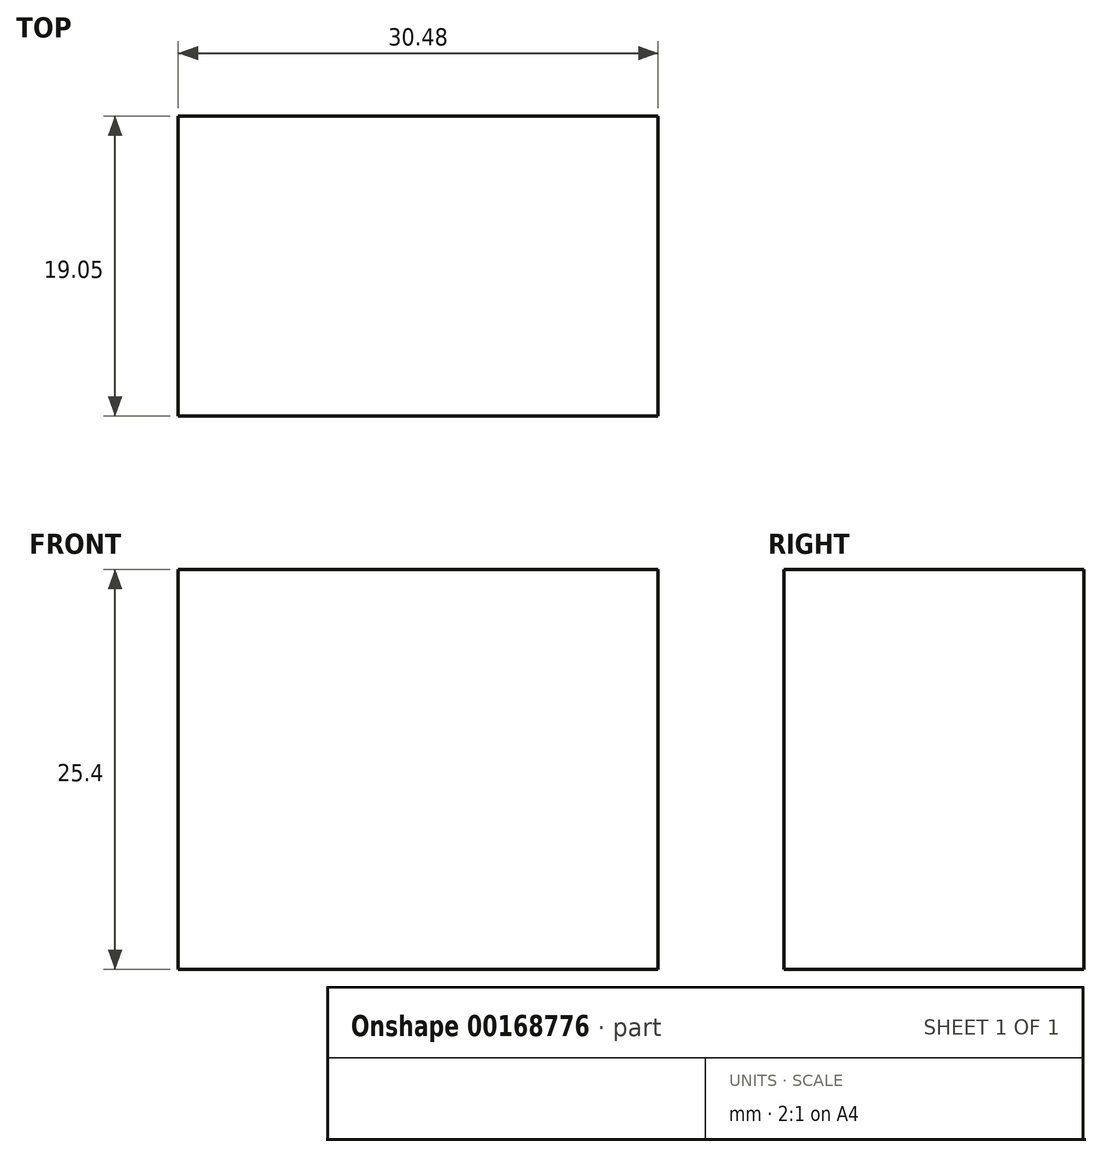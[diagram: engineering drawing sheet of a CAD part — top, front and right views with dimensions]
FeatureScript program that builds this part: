
annotation { "Feature Type Name" : "Feature", "Feature Type Description" : "" }
export const myFeature = defineFeature(function(context is Context, id is Id, definition is map)
    precondition{}
    {
        {
            var Q0;
            Q0=qCreatedBy(makeId("Front.planeOp"),FACE);
            var sketch = newSketch(context, id + "F0", { "sketchPlane" : qUnion([Q0])});
            skLineSegment(sketch, "E0.bottom", {"start": v(9.52, -12.7) * mm, "end": v(-9.53, -12.7) * mm});
            skLineSegment(sketch, "E0.top", {"start": v(9.52, 12.7) * mm, "end": v(-9.53, 12.7) * mm});
            skLineSegment(sketch, "E0.left", {"start": v(9.52, -12.7) * mm, "end": v(9.52, 12.7) * mm});
            skLineSegment(sketch, "E0.right", {"start": v(-9.53, -12.7) * mm, "end": v(-9.53, 12.7) * mm});
            skPoint(sketch, "E0.middle", {"position": v(0, 0) * mm});
            skLineSegment(sketch, "E1", {"start": v(-9.53, 11.43) * mm, "end": v(9.52, 11.43) * mm});
            skLineSegment(sketch, "E2", {"start": v(-9.53, 10.16) * mm, "end": v(9.52, 10.16) * mm});
            skLineSegment(sketch, "E3", {"start": v(-9.53, 8.89) * mm, "end": v(9.52, 8.89) * mm});
            skLineSegment(sketch, "E4", {"start": v(-9.53, 7.62) * mm, "end": v(9.52, 7.62) * mm});
            skLineSegment(sketch, "E5", {"start": v(-9.53, 6.35) * mm, "end": v(9.52, 6.35) * mm});
            skLineSegment(sketch, "E6", {"start": v(-9.53, 5.08) * mm, "end": v(9.52, 5.08) * mm});
            skLineSegment(sketch, "E7", {"start": v(-9.53, 3.8) * mm, "end": v(9.53, 3.8) * mm});
            skLineSegment(sketch, "E8", {"start": v(-9.53, 2.54) * mm, "end": v(9.53, 2.54) * mm});
            skLineSegment(sketch, "E9", {"start": v(-9.53, 1.27) * mm, "end": v(9.53, 1.27) * mm});
            skLineSegment(sketch, "E10", {"start": v(-9.53, 0) * mm, "end": v(9.52, 0) * mm});
            skLineSegment(sketch, "E11", {"start": v(-9.53, -1.27) * mm, "end": v(9.53, -1.27) * mm});
            skLineSegment(sketch, "E12", {"start": v(-9.53, -2.54) * mm, "end": v(9.53, -2.54) * mm});
            skLineSegment(sketch, "E13", {"start": v(-9.53, -3.81) * mm, "end": v(9.53, -3.81) * mm});
            skLineSegment(sketch, "E14", {"start": v(-9.53, -5.08) * mm, "end": v(9.53, -5.08) * mm});
            skLineSegment(sketch, "E15", {"start": v(-9.52, -6.35) * mm, "end": v(9.53, -6.35) * mm});
            skLineSegment(sketch, "E16", {"start": v(-9.53, -7.62) * mm, "end": v(9.53, -7.62) * mm});
            skLineSegment(sketch, "E17", {"start": v(-9.52, -8.9) * mm, "end": v(9.53, -8.9) * mm});
            skLineSegment(sketch, "E18", {"start": v(-9.53, -10.16) * mm, "end": v(9.53, -10.16) * mm});
            skLineSegment(sketch, "E19", {"start": v(-9.52, -11.43) * mm, "end": v(9.53, -11.43) * mm});
            skLineSegment(sketch, "E20", {"start": v(-9.52, -10.16) * mm, "end": v(9.53, -10.16) * mm});
            skSolve(sketch);
        }
        {
            var Q0;
            Q0=sQuery(id+"F0.wireOp",EDGE,"E0.left");
            var Q1;
            Q1=sQuery(id+"F0.wireOp",EDGE,"E0.top");
            var Q2;
            Q2=sQuery(id+"F0.wireOp",EDGE,"E0.right");
            var Q3;
            Q3=sQuery(id+"F0.wireOp",EDGE,"E0.bottom");
            extrude(context, id + "F1", {"bodyType" : ToolBodyType.SURFACE, "surfaceEntities" : qUnion([Q0, Q1, Q2, Q3]), "endBound" : BoundingType.SYMMETRIC, "depth" : 25.4 * mm});
        }
        {
            var Q0;
            Q0=sQuery(id+"F0.wireOp",EDGE,"E1");
            var Q1;
            Q1=sQuery(id+"F0.wireOp",EDGE,"E2");
            var Q2;
            Q2=sQuery(id+"F0.wireOp",EDGE,"E3");
            var Q3;
            Q3=sQuery(id+"F0.wireOp",EDGE,"E4");
            var Q4;
            Q4=sQuery(id+"F0.wireOp",EDGE,"E5");
            var Q5;
            Q5=sQuery(id+"F0.wireOp",EDGE,"E6");
            var Q6;
            Q6=sQuery(id+"F0.wireOp",EDGE,"E7");
            var Q7;
            Q7=sQuery(id+"F0.wireOp",EDGE,"E8");
            var Q8;
            Q8=sQuery(id+"F0.wireOp",EDGE,"E9");
            var Q9;
            Q9=sQuery(id+"F0.wireOp",EDGE,"E10");
            var Q10;
            Q10=sQuery(id+"F0.wireOp",EDGE,"E11");
            var Q11;
            Q11=sQuery(id+"F0.wireOp",EDGE,"E12");
            var Q12;
            Q12=sQuery(id+"F0.wireOp",EDGE,"E13");
            var Q13;
            Q13=sQuery(id+"F0.wireOp",EDGE,"E14");
            var Q14;
            Q14=sQuery(id+"F0.wireOp",EDGE,"E15");
            var Q15;
            Q15=sQuery(id+"F0.wireOp",EDGE,"E16");
            var Q16;
            Q16=sQuery(id+"F0.wireOp",EDGE,"E17");
            var Q17;
            Q17=sQuery(id+"F0.wireOp",EDGE,"E18");
            var Q18;
            Q18=sQuery(id+"F0.wireOp",EDGE,"E19");
            extrude(context, id + "F2", {"bodyType" : ToolBodyType.SURFACE, "surfaceEntities" : qUnion([Q0, Q1, Q2, Q3, Q4, Q5, Q6, Q7, Q8, Q9, Q10, Q11, Q12, Q13, Q14, Q15, Q16, Q17, Q18]), "endBound" : BoundingType.SYMMETRIC, "depth" : 20.32 * mm});
        }
        {
            var Q0;
            {var subQ0=sQuery(id+"F0.wireOp",EDGE,"E0.top");Q0=makeQuery(id+"F0.imprint","IMPRINT",FACE,{"disambiguationData":[TD([[makeQuery(id+"F0.imprint","IMPRINT",EDGE,{"derivedFrom":subQ0}),1.0]])]});}
            var Q1;
            {var subQ0=sQuery(id+"F0.wireOp",EDGE,"E1");Q1=makeQuery(id+"F0.imprint","IMPRINT",FACE,{"disambiguationData":[TD([[makeQuery(id+"F0.imprint","IMPRINT",EDGE,{"derivedFrom":subQ0}),-1.0]])]});}
            var Q2;
            {var subQ0=sQuery(id+"F0.wireOp",EDGE,"E2");Q2=makeQuery(id+"F0.imprint","IMPRINT",FACE,{"disambiguationData":[TD([[makeQuery(id+"F0.imprint","IMPRINT",EDGE,{"derivedFrom":subQ0}),-1.0]])]});}
            var Q3;
            {var subQ0=sQuery(id+"F0.wireOp",EDGE,"E3");Q3=makeQuery(id+"F0.imprint","IMPRINT",FACE,{"disambiguationData":[TD([[makeQuery(id+"F0.imprint","IMPRINT",EDGE,{"derivedFrom":subQ0}),-1.0]])]});}
            var Q4;
            {var subQ0=sQuery(id+"F0.wireOp",EDGE,"E4");Q4=makeQuery(id+"F0.imprint","IMPRINT",FACE,{"disambiguationData":[TD([[makeQuery(id+"F0.imprint","IMPRINT",EDGE,{"derivedFrom":subQ0}),-1.0]])]});}
            var Q5;
            {var subQ0=sQuery(id+"F0.wireOp",EDGE,"E5");Q5=makeQuery(id+"F0.imprint","IMPRINT",FACE,{"disambiguationData":[TD([[makeQuery(id+"F0.imprint","IMPRINT",EDGE,{"derivedFrom":subQ0}),-1.0]])]});}
            var Q6;
            {var subQ0=sQuery(id+"F0.wireOp",EDGE,"E6");Q6=makeQuery(id+"F0.imprint","IMPRINT",FACE,{"disambiguationData":[TD([[makeQuery(id+"F0.imprint","IMPRINT",EDGE,{"derivedFrom":subQ0}),-1.0]])]});}
            var Q7;
            {var subQ0=sQuery(id+"F0.wireOp",EDGE,"E7");Q7=makeQuery(id+"F0.imprint","IMPRINT",FACE,{"disambiguationData":[TD([[makeQuery(id+"F0.imprint","IMPRINT",EDGE,{"derivedFrom":subQ0}),-1.0]])]});}
            var Q8;
            {var subQ0=sQuery(id+"F0.wireOp",EDGE,"E8");Q8=makeQuery(id+"F0.imprint","IMPRINT",FACE,{"disambiguationData":[TD([[makeQuery(id+"F0.imprint","IMPRINT",EDGE,{"derivedFrom":subQ0}),-1.0]])]});}
            var Q9;
            {var subQ0=sQuery(id+"F0.wireOp",EDGE,"E9");Q9=makeQuery(id+"F0.imprint","IMPRINT",FACE,{"disambiguationData":[TD([[makeQuery(id+"F0.imprint","IMPRINT",EDGE,{"derivedFrom":subQ0}),-1.0]])]});}
            var Q10;
            {var subQ0=sQuery(id+"F0.wireOp",EDGE,"E10");Q10=makeQuery(id+"F0.imprint","IMPRINT",FACE,{"disambiguationData":[TD([[makeQuery(id+"F0.imprint","IMPRINT",EDGE,{"derivedFrom":subQ0}),-1.0]])]});}
            var Q11;
            {var subQ0=sQuery(id+"F0.wireOp",EDGE,"E11");Q11=makeQuery(id+"F0.imprint","IMPRINT",FACE,{"disambiguationData":[TD([[makeQuery(id+"F0.imprint","IMPRINT",EDGE,{"derivedFrom":subQ0}),-1.0]])]});}
            var Q12;
            {var subQ0=sQuery(id+"F0.wireOp",EDGE,"E12");Q12=makeQuery(id+"F0.imprint","IMPRINT",FACE,{"disambiguationData":[TD([[makeQuery(id+"F0.imprint","IMPRINT",EDGE,{"derivedFrom":subQ0}),-1.0]])]});}
            var Q13;
            {var subQ0=sQuery(id+"F0.wireOp",EDGE,"E13");Q13=makeQuery(id+"F0.imprint","IMPRINT",FACE,{"disambiguationData":[TD([[makeQuery(id+"F0.imprint","IMPRINT",EDGE,{"derivedFrom":subQ0}),-1.0]])]});}
            var Q14;
            {var subQ0=sQuery(id+"F0.wireOp",EDGE,"E14");Q14=makeQuery(id+"F0.imprint","IMPRINT",FACE,{"disambiguationData":[TD([[makeQuery(id+"F0.imprint","IMPRINT",EDGE,{"derivedFrom":subQ0}),-1.0]])]});}
            var Q15;
            {var subQ0=sQuery(id+"F0.wireOp",EDGE,"E15");Q15=makeQuery(id+"F0.imprint","IMPRINT",FACE,{"disambiguationData":[TD([[makeQuery(id+"F0.imprint","IMPRINT",EDGE,{"derivedFrom":subQ0}),-1.0]])]});}
            var Q16;
            {var subQ0=sQuery(id+"F0.wireOp",EDGE,"E16");Q16=makeQuery(id+"F0.imprint","IMPRINT",FACE,{"disambiguationData":[TD([[makeQuery(id+"F0.imprint","IMPRINT",EDGE,{"derivedFrom":subQ0}),-1.0]])]});}
            var Q17;
            {var subQ0=sQuery(id+"F0.wireOp",EDGE,"E17");Q17=makeQuery(id+"F0.imprint","IMPRINT",FACE,{"disambiguationData":[TD([[makeQuery(id+"F0.imprint","IMPRINT",EDGE,{"derivedFrom":subQ0}),-1.0]])]});}
            var Q18;
            {var subQ0=sQuery(id+"F0.wireOp",EDGE,"E19");Q18=makeQuery(id+"F0.imprint","IMPRINT",FACE,{"disambiguationData":[TD([[makeQuery(id+"F0.imprint","IMPRINT",EDGE,{"derivedFrom":subQ0}),1.0]])]});}
            var Q19;
            {var subQ0=sQuery(id+"F0.wireOp",EDGE,"E0.bottom");Q19=makeQuery(id+"F0.imprint","IMPRINT",FACE,{"disambiguationData":[TD([[makeQuery(id+"F0.imprint","IMPRINT",EDGE,{"derivedFrom":subQ0}),-1.0]])]});}
            extrude(context, id + "F3", {"entities" : qUnion([Q0, Q1, Q2, Q3, Q4, Q5, Q6, Q7, Q8, Q9, Q10, Q11, Q12, Q13, Q14, Q15, Q16, Q17, Q18, Q19]), "endBound" : BoundingType.SYMMETRIC, "depth" : 30.48 * mm});
        }
        {
            var Q0;
            Q0=makeQuery(id+"F2.opExtrude","SWEPT_BODY",BODY,{"disambiguationData":[OSD([sQuery(id+"F0.wireOp",EDGE,"E5")])]});
            var Q1;
            Q1=makeQuery(id+"F1.opExtrude","SWEPT_BODY",BODY,{"disambiguationData":[OSD([sQuery(id+"F0.wireOp",EDGE,"E0.bottom")])]});
            var Q2;
            Q2=makeQuery(id+"F2.opExtrude","SWEPT_BODY",BODY,{"disambiguationData":[OSD([sQuery(id+"F0.wireOp",EDGE,"E6")])]});
            var Q3;
            Q3=makeQuery(id+"F2.opExtrude","SWEPT_BODY",BODY,{"disambiguationData":[OSD([sQuery(id+"F0.wireOp",EDGE,"E7")])]});
            var Q4;
            Q4=makeQuery(id+"F2.opExtrude","SWEPT_BODY",BODY,{"disambiguationData":[OSD([sQuery(id+"F0.wireOp",EDGE,"E16")])]});
            var Q5;
            Q5=makeQuery(id+"F2.opExtrude","SWEPT_BODY",BODY,{"disambiguationData":[OSD([sQuery(id+"F0.wireOp",EDGE,"E14")])]});
            var Q6;
            Q6=makeQuery(id+"F2.opExtrude","SWEPT_BODY",BODY,{"disambiguationData":[OSD([sQuery(id+"F0.wireOp",EDGE,"E15")])]});
            var Q7;
            Q7=makeQuery(id+"F2.opExtrude","SWEPT_BODY",BODY,{"disambiguationData":[OSD([sQuery(id+"F0.wireOp",EDGE,"E19")])]});
            var Q8;
            Q8=makeQuery(id+"F2.opExtrude","SWEPT_BODY",BODY,{"disambiguationData":[OSD([sQuery(id+"F0.wireOp",EDGE,"E18")])]});
            var Q9;
            Q9=makeQuery(id+"F2.opExtrude","SWEPT_BODY",BODY,{"disambiguationData":[OSD([sQuery(id+"F0.wireOp",EDGE,"E17")])]});
            var Q10;
            Q10=makeQuery(id+"F2.opExtrude","SWEPT_BODY",BODY,{"disambiguationData":[OSD([sQuery(id+"F0.wireOp",EDGE,"E12")])]});
            var Q11;
            Q11=makeQuery(id+"F2.opExtrude","SWEPT_BODY",BODY,{"disambiguationData":[OSD([sQuery(id+"F0.wireOp",EDGE,"E11")])]});
            var Q12;
            Q12=makeQuery(id+"F2.opExtrude","SWEPT_BODY",BODY,{"disambiguationData":[OSD([sQuery(id+"F0.wireOp",EDGE,"E13")])]});
            var Q13;
            Q13=makeQuery(id+"F2.opExtrude","SWEPT_BODY",BODY,{"disambiguationData":[OSD([sQuery(id+"F0.wireOp",EDGE,"E8")])]});
            var Q14;
            Q14=makeQuery(id+"F2.opExtrude","SWEPT_BODY",BODY,{"disambiguationData":[OSD([sQuery(id+"F0.wireOp",EDGE,"E10")])]});
            var Q15;
            Q15=makeQuery(id+"F2.opExtrude","SWEPT_BODY",BODY,{"disambiguationData":[OSD([sQuery(id+"F0.wireOp",EDGE,"E9")])]});
            var Q16;
            Q16=makeQuery(id+"F2.opExtrude","SWEPT_BODY",BODY,{"disambiguationData":[OSD([sQuery(id+"F0.wireOp",EDGE,"E4")])]});
            var Q17;
            Q17=makeQuery(id+"F2.opExtrude","SWEPT_BODY",BODY,{"disambiguationData":[OSD([sQuery(id+"F0.wireOp",EDGE,"E1")])]});
            var Q18;
            Q18=makeQuery(id+"F2.opExtrude","SWEPT_BODY",BODY,{"disambiguationData":[OSD([sQuery(id+"F0.wireOp",EDGE,"E3")])]});
            var Q19;
            Q19=makeQuery(id+"F2.opExtrude","SWEPT_BODY",BODY,{"disambiguationData":[OSD([sQuery(id+"F0.wireOp",EDGE,"E2")])]});
            var Q20;
            Q20=makeQuery(id+"F3.opExtrude","SWEPT_BODY",BODY,{"disambiguationData":[OSD([sQuery(id+"F0.wireOp",EDGE,"E0.bottom"),sQuery(id+"F0.wireOp",EDGE,"E0.top"),sQuery(id+"F0.wireOp",EDGE,"E0.left"),sQuery(id+"F0.wireOp",EDGE,"E0.right")])]});
            var Q21;
            Q21=makeQuery(id+"F3.opExtrude","CAP_EDGE",EDGE,{"disambiguationData":[OSD([sQuery(id+"F0.wireOp",EDGE,"E0.left")])],"isStart":true});
            transform(context, id + "F4", {"entities" : qUnion([Q0, Q1, Q2, Q3, Q4, Q5, Q6, Q7, Q8, Q9, Q10, Q11, Q12, Q13, Q14, Q15, Q16, Q17, Q18, Q19, Q20]), "transformType" : TransformType.ROTATION, "transformAxis" : qUnion([Q21]), "angle" : 90 * degree, "makeCopy" : false});
        }
    });
